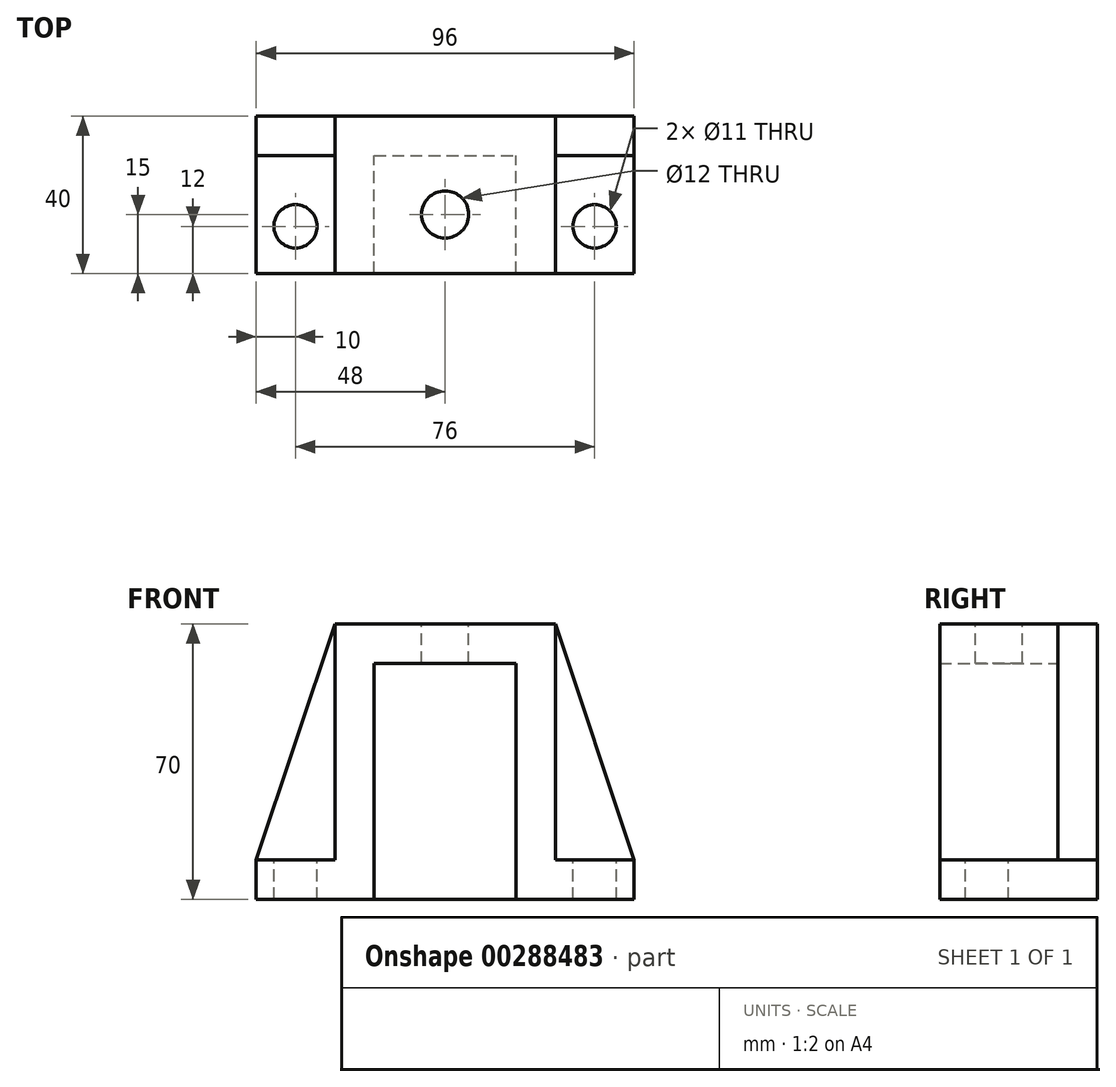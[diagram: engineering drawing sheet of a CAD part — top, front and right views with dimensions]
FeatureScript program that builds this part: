
annotation { "Feature Type Name" : "Feature", "Feature Type Description" : "" }
export const myFeature = defineFeature(function(context is Context, id is Id, definition is map)
    precondition{}
    {
        {
            var Q0;
            Q0=qCreatedBy(makeId("Front.planeOp"),FACE);
            var sketch = newSketch(context, id + "F0", { "sketchPlane" : qUnion([Q0])});
            skLineSegment(sketch, "E0", {"start": v(-48, -35) * mm, "end": v(48, -35) * mm});
            skLineSegment(sketch, "E1", {"start": v(48, -35) * mm, "end": v(48, -25) * mm});
            skLineSegment(sketch, "E2", {"start": v(28, 35) * mm, "end": v(-28, 35) * mm});
            skLineSegment(sketch, "E3", {"start": v(-48, -35) * mm, "end": v(-48, -25) * mm});
            skLineSegment(sketch, "E4", {"start": v(-48, -25) * mm, "end": v(-28, -25) * mm});
            skLineSegment(sketch, "E5", {"start": v(-28, -25) * mm, "end": v(-28, 35) * mm});
            skLineSegment(sketch, "E6", {"start": v(28, 35) * mm, "end": v(28, -25) * mm});
            skLineSegment(sketch, "E7", {"start": v(28, -25) * mm, "end": v(48, -25) * mm});
            skLineSegment(sketch, "E8", {"start": v(-18, -35) * mm, "end": v(-18, 25) * mm});
            skLineSegment(sketch, "E9", {"start": v(-18, 25) * mm, "end": v(18, 25) * mm});
            skLineSegment(sketch, "E10", {"start": v(18, 25) * mm, "end": v(18, -35) * mm});
            skLineSegment(sketch, "E11", {"start": v(-28, 35) * mm, "end": v(-48, -25) * mm});
            skLineSegment(sketch, "E12", {"start": v(28, 35) * mm, "end": v(48, -25) * mm});
            skSolve(sketch);
        }
        {
            var Q0;
            {var subQ3=sQuery(id+"F0.wireOp",EDGE,"E1");Q0=makeQuery(id+"F0.imprint","IMPRINT",FACE,{"disambiguationData":[TD([[makeQuery(id+"F0.imprint","IMPRINT",EDGE,{"derivedFrom":subQ3}),1.0]])]});}
            extrude(context, id + "F1", {"entities" : qUnion([Q0]), "depth" : 40 * mm});
        }
        {
            var Q0;
            Q0=makeQuery(id+"F0.imprint","IMPRINT",FACE,{"disambiguationData":[TD([[makeQuery(id+"F0.imprint","IMPRINT",EDGE,{"derivedFrom":sQuery(id+"F0.wireOp",EDGE,"E4")}),1.0]])]});
            var Q1;
            Q1=makeQuery(id+"F0.imprint","IMPRINT",FACE,{"disambiguationData":[TD([[makeQuery(id+"F0.imprint","IMPRINT",EDGE,{"derivedFrom":sQuery(id+"F0.wireOp",EDGE,"E6")}),1.0]])]});
            var Q2;
            {var subQ0=sQuery(id+"F0.wireOp",EDGE,"E8");Q2=makeQuery(id+"F0.imprint","IMPRINT",FACE,{"disambiguationData":[TD([[makeQuery(id+"F0.imprint","IMPRINT",EDGE,{"derivedFrom":subQ0}),-1.0]])]});}
            extrude(context, id + "F2", {"entities" : qUnion([Q0, Q1, Q2]), "operationType" : NewBodyOperationType.ADD, "depth" : 10 * mm});
        }
        {
            var Q0;
            Q0=makeQuery(id+"F1.opExtrude","SWEPT_FACE",FACE,{"disambiguationData":[OSD([sQuery(id+"F0.wireOp",EDGE,"E2")])]});
            var sketch = newSketch(context, id + "F3", { "sketchPlane" : qUnion([Q0])});
            skCircle(sketch, "E13", {"center": v(0, -25) * mm, "radius": 6 * mm});
            skPoint(sketch, "E13.centerSnap0", {"position": v(0, -40) * mm});
            skCircle(sketch, "E14", {"center": v(38, -28) * mm, "radius": 5.5 * mm});
            skCircle(sketch, "E15", {"center": v(-38, -28) * mm, "radius": 5.5 * mm});
            skSolve(sketch);
        }
        {
            var Q0;
            Q0=makeQuery(id+"F3.imprint","IMPRINT",FACE,{"disambiguationData":[TD([[makeQuery(id+"F3.imprint","IMPRINT",EDGE,{"derivedFrom":sQuery(id+"F3.wireOp",EDGE,"E14")}),1.0]])]});
            var Q1;
            Q1=makeQuery(id+"F3.imprint","IMPRINT",FACE,{"disambiguationData":[TD([[makeQuery(id+"F3.imprint","IMPRINT",EDGE,{"derivedFrom":sQuery(id+"F3.wireOp",EDGE,"E13")}),1.0]])]});
            var Q2;
            Q2=makeQuery(id+"F3.imprint","IMPRINT",FACE,{"disambiguationData":[TD([[makeQuery(id+"F3.imprint","IMPRINT",EDGE,{"derivedFrom":sQuery(id+"F3.wireOp",EDGE,"E15")}),1.0]])]});
            var Q3;
            Q3=sQuery(id+"F3.wireOp",EDGE,"E13");
            var Q4;
            Q4=sQuery(id+"F3.wireOp",EDGE,"E14");
            var Q5;
            Q5=sQuery(id+"F3.wireOp",EDGE,"E15");
            extrude(context, id + "F4", {"entities" : qUnion([Q0, Q1, Q2]), "operationType" : NewBodyOperationType.REMOVE, "surfaceEntities" : qUnion([Q3, Q4, Q5]), "oppositeDirection" : true, "depth" : 75 * mm});
        }
    });
